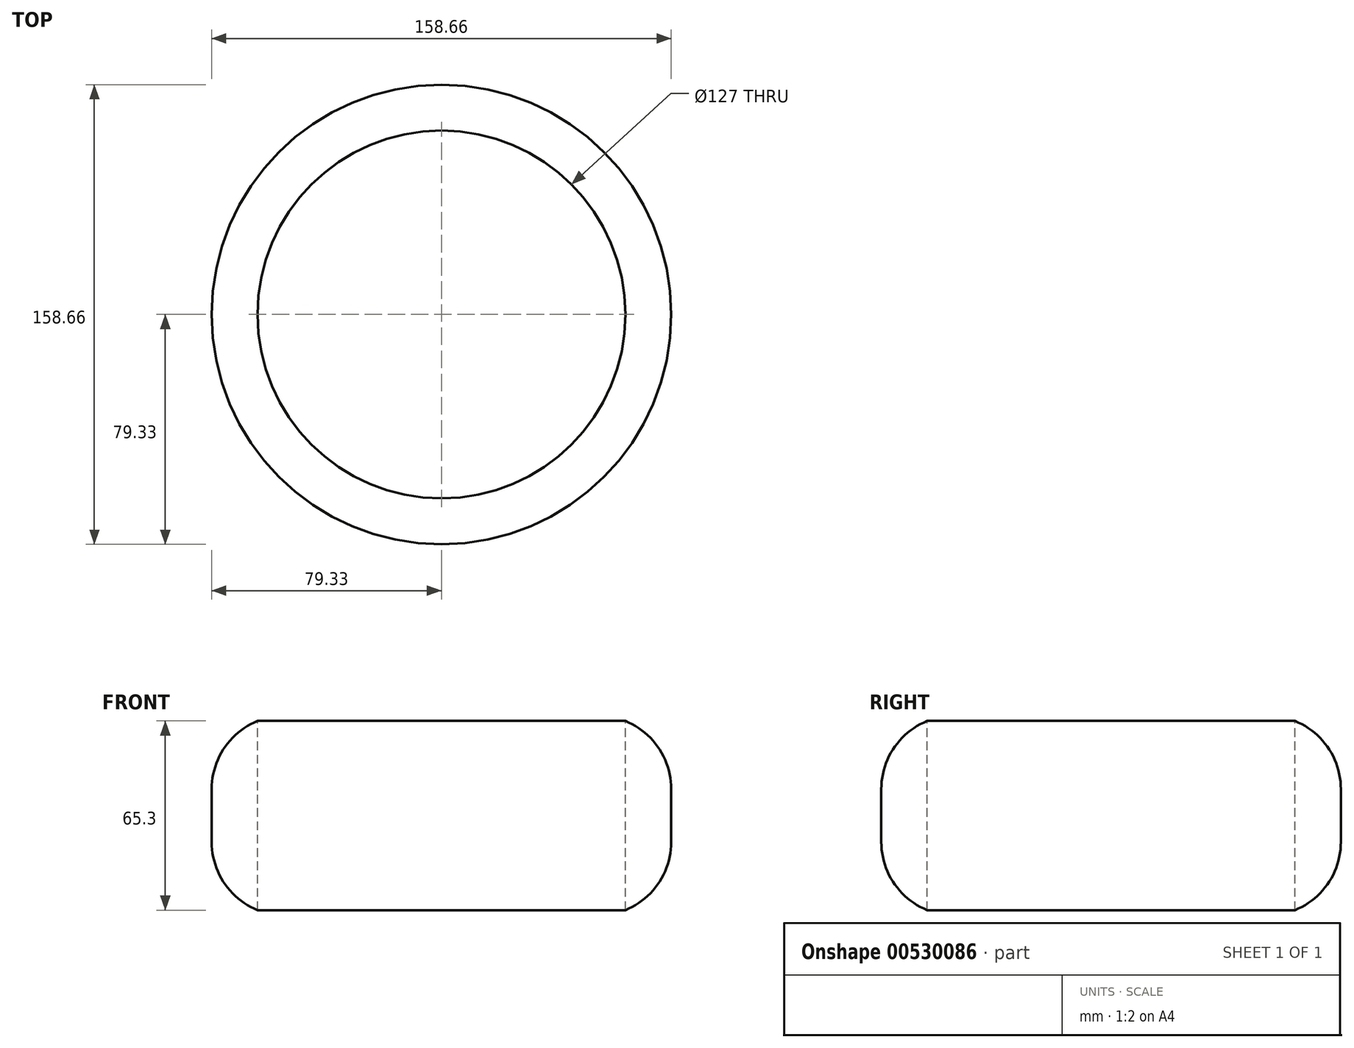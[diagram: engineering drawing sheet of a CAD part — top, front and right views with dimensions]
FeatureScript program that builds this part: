
annotation { "Feature Type Name" : "Feature", "Feature Type Description" : "" }
export const myFeature = defineFeature(function(context is Context, id is Id, definition is map)
    precondition{}
    {
        {
            var Q0;
            Q0=qCreatedBy(makeId("Front.planeOp"),FACE);
            var sketch = newSketch(context, id + "F0", { "sketchPlane" : qUnion([Q0])});
            skLineSegment(sketch, "E0.bottom", {"start": v(0, 0) * mm, "end": v(79.33, 0) * mm});
            skLineSegment(sketch, "E0.top", {"start": v(0, 69.04) * mm, "end": v(79.33, 69.04) * mm});
            skLineSegment(sketch, "E0.left", {"start": v(0, 0) * mm, "end": v(0, 69.04) * mm});
            skLineSegment(sketch, "E0.right", {"start": v(79.33, 0) * mm, "end": v(79.33, 69.04) * mm});
            skLineSegment(sketch, "E1.bottom", {"start": v(79.33, 34.52) * mm, "end": v(79.33, 34.52) * mm});
            skLineSegment(sketch, "E1.top", {"start": v(79.33, 34.52) * mm, "end": v(79.33, 34.52) * mm});
            skLineSegment(sketch, "E1.left", {"start": v(79.33, 34.52) * mm, "end": v(79.33, 34.52) * mm});
            skLineSegment(sketch, "E1.right", {"start": v(79.33, 34.52) * mm, "end": v(79.33, 34.52) * mm});
            skSolve(sketch);
        }
        {
            var Q0;
            Q0 = qSketchRegion(id + "F0", true);
            var Q1;
            Q1=sQuery(id+"F0.wireOp",EDGE,"E0.left");
            revolve(context, id + "F1", {"entities" : qUnion([Q0]), "axis" : qUnion([Q1]), "revolveType" : RevolveType.FULL});
        }
        {
            var Q0;
            Q0=makeQuery(id+"F1.opRevolve","SWEPT_FACE",FACE,{"disambiguationData":[OSD([sQuery(id+"F0.wireOp",EDGE,"E0.right")])]});
            fillet(context, id + "F2", {"entities" : qUnion([Q0]), "radius" : 25.4 * mm, "tangentPropagation" : true, "allowEdgeOverflow" : false});
        }
        {
            var Q0;
            Q0=makeQuery(id+"F1.opRevolve","SWEPT_FACE",FACE,{"disambiguationData":[OSD([sQuery(id+"F0.wireOp",EDGE,"E0.top")])]});
            extrude(context, id + "F3", {"entities" : qUnion([Q0]), "operationType" : NewBodyOperationType.ADD, "depth" : 25.4 * mm, "offsetDistance" : 25.4 * mm});
        }
        {
            var Q0;
            Q0=makeQuery(id+"F3.opExtrude","CAP_FACE",FACE,{"disambiguationData":[OSD([sQuery(id+"F0.wireOp",EDGE,"E0.top")])],"isStart":false});
            var sketch = newSketch(context, id + "F4", { "sketchPlane" : qUnion([Q0])});
            skPoint(sketch, "E2", {"position": v(0, 0) * mm});
            skSolve(sketch);
        }
        {
            var Q0;
            Q0=sQuery(id+"F4.wireOp",VERTEX,"E2");
            var Q1;
            Q1=makeQuery(id+"F1.opRevolve","SWEPT_BODY",BODY,{"disambiguationData":[OSD([sQuery(id+"F0.wireOp",EDGE,"E0.bottom"),sQuery(id+"F0.wireOp",EDGE,"E0.top"),sQuery(id+"F0.wireOp",EDGE,"E0.left"),sQuery(id+"F0.wireOp",EDGE,"E0.right")])]});
            hole(context, id + "F5", {"style" : HoleStyle.SIMPLE, "endStyle" : HoleEndStyle.THROUGH, "holeDiameter" : 127 * mm, "isTappedThrough" : true, "tappedDepth" : 12.7 * mm, "tapClearance" : 3, "locations" : qUnion([Q0]), "scope" : qUnion([Q1])});
        }
    });
